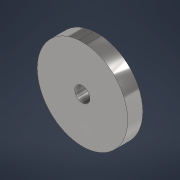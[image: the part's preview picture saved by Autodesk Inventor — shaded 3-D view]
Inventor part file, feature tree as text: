
AUTODESK INVENTOR PART (.ipt)
format: ipt  version: 2021 (Build 250183000, 183)  size: 106,496 bytes
history: native  units: mm
features: sketch x3, extrude x2, hole x1
ambient origin geometry x8: Origin, YZ Plane, XZ Plane, XY Plane, X Axis, Y Axis, Z Axis, Center Point
bodies: Solid1 (feature_tree)
feature tree (6):
  extrude  "Extrusion1"  Depth=10.0mm
  extrude  "Extrusion2"  Depth=10.0mm TaperAngle=0.0deg
  hole  "Hole1"  [1 undecoded]
  sketch  "Sketch1"  dims[d0=10.0mm d1=0.0mm d2=60.0mm]
  sketch  "Sketch2"  dims[d3=5.0mm d4=10.0mm d5=0.0mm]
  sketch  "Sketch3"  dims[d6=10.0mm d7=6.0mm d8=4.0mm d9=2.0mm d10=90.0deg d11=8.0mm d12=20.594885mm]
note: 1 required parameter value undecoded (feature->parameter linkage not recoverable at this tier; creation-order binding heuristic only, values carry confidence <= 0.55)
